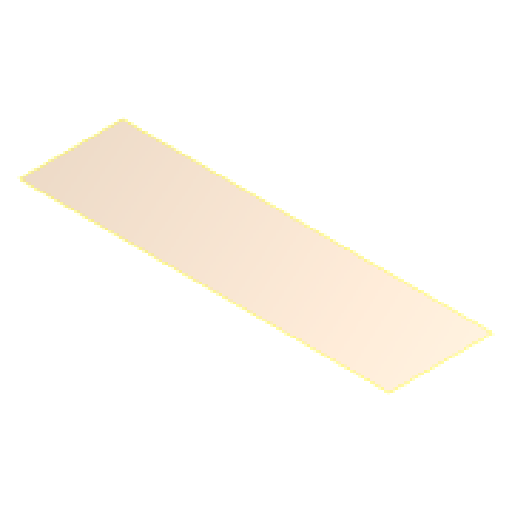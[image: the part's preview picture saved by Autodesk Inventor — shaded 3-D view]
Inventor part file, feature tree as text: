
AUTODESK INVENTOR PART (.ipt)
format: ipt  version: 2024.1 (Build 281209000, 209)  size: 212,480 bytes
history: native  units: mm
features: sketch x5, other x5, reference x4, plane x2, extrude x2, hole x2, projected_geometry x2, chamfer x1
ambient origin geometry x8: Origin, YZ Plane, XZ Plane, XY Plane, X Axis, Y Axis, Z Axis, Center Point
bodies: Body1 (feature_tree)
feature tree (23):
  plane  "Arbeitsebene1"
  plane  "Arbeitsebene2"
  extrude  "Extrusion6"  Depth=10.0mm
  extrude  "Extrusion7"  Depth=5.0mm
  chamfer  "Fasen2"  Distance=5.0mm
  hole  "Bohrung3"  [1 undecoded]
  sketch  "Skizze11"  dims[d44=3.6mm d45=6.0mm d46=4.0mm d47=2.0mm d48=90.0deg d49=15.0mm d50=20.594885mm d51=36.0mm]
  hole  "Bohrung4"  [1 undecoded]
  sketch  "Skizze8"  dims[d34=10.0mm d35=0.0mm d36=20.0mm]
  reference  "Referenz12"
  reference  "Referenz13"
  reference  "Referenz14"
  sketch  "Skizze9"  dims[d37=0.5mm d38=5.0mm d39=5.0mm d40=0.0mm]
  reference  "Referenz15"
  sketch  "Skizze10"  dims[d41=2.0mm d42=2.0mm d43=45.0deg]
  projected_geometry  "Projizierte Kontur7"
  sketch  "Skizze12"  dims[d52=28.0mm d53=2.8mm d54=6.0mm d55=4.0mm d56=2.0mm d57=90.0deg d58=15.0mm d59=20.594885mm d21=0.5mm d22=0.872665mm d23=0.5mm d24=0.872665mm d27=0.5mm d28=0.872665mm d29=0.5mm d30=0.872665mm]
  projected_geometry  "Projizierte Kontur8"
  other  "Assembly_Planktoscope_Uc2version_wormdrive_V3.iam"
  other  "60_Planktoscope_Base_half_wormdrive_1:1"
  other  "60_Planktoscope_Base_half_wormdrive_1_MIR:1"
  other  "00_Microscope_Slide:1"
  other  "60_Planktoscope_Base_half1_MIR:1"
note: 2 required parameter values undecoded (feature->parameter linkage not recoverable at this tier; creation-order binding heuristic only, values carry confidence <= 0.55)
